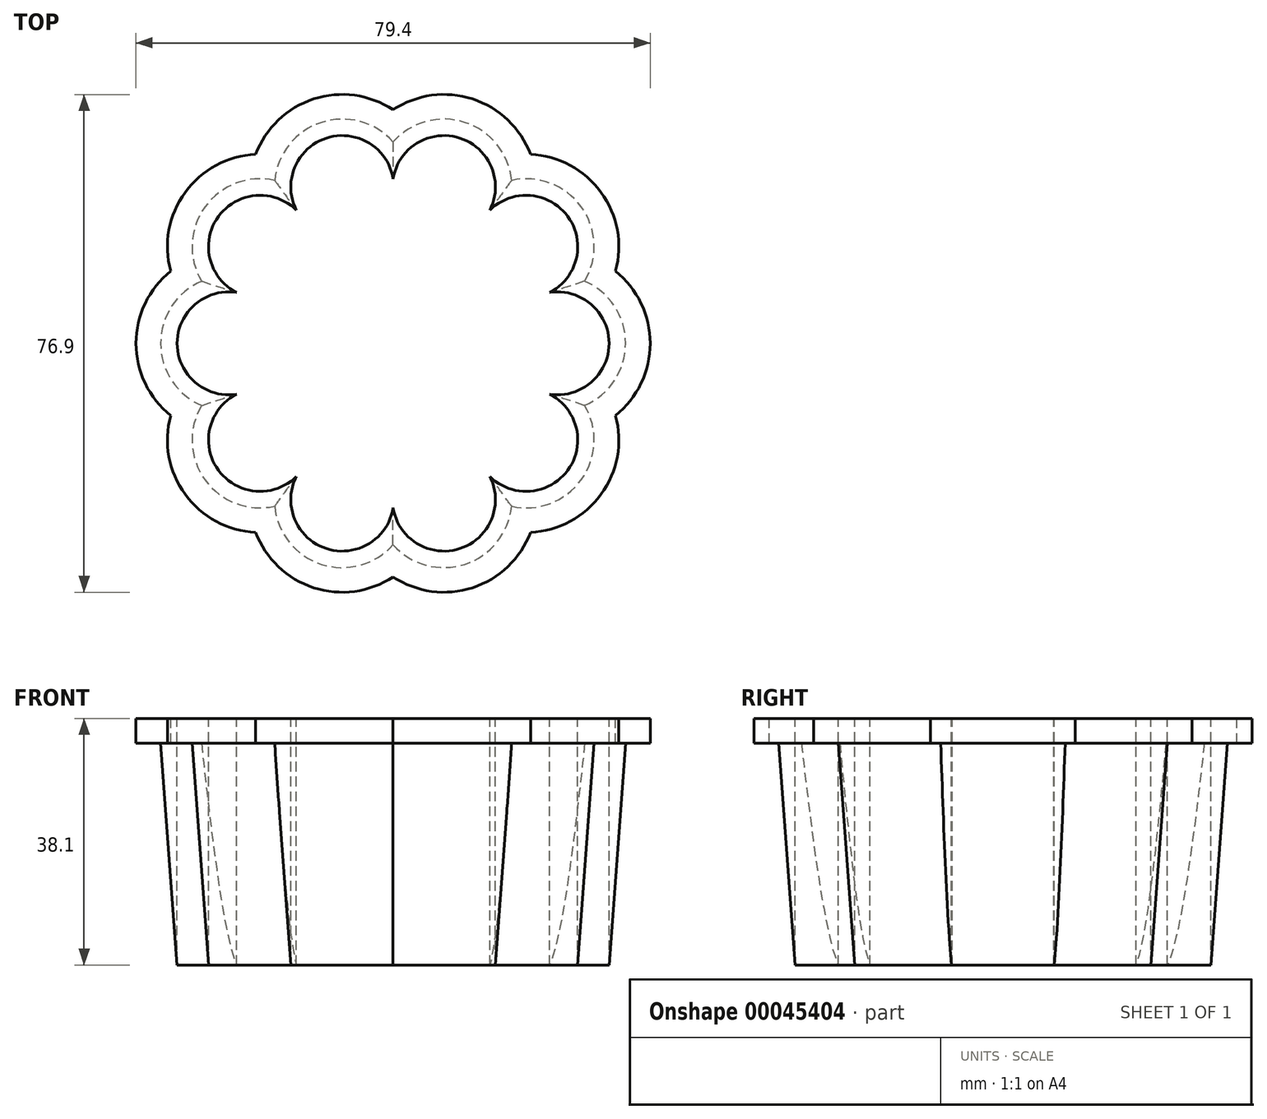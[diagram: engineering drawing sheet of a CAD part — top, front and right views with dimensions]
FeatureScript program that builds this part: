
annotation { "Feature Type Name" : "Feature", "Feature Type Description" : "" }
export const myFeature = defineFeature(function(context is Context, id is Id, definition is map)
    precondition{}
    {
        {
            var Q0;
            Q0=qCreatedBy(makeId("Top.planeOp"),FACE);
            var sketch = newSketch(context, id + "F0", { "sketchPlane" : qUnion([Q0])});
            skCircle(sketch, "E0", {"center": v(0, 0) * mm, "radius": 25.4 * mm, "construction": true});
            skArc(sketch, "E1", {"start": v(-24.16, -7.85) * mm, "mid": v(-26.98, -19.6) * mm, "end": v(-14.93, -20.55) * mm});
            skArc(sketch, "E2.1.0", {"start": v(-24.16, 7.85) * mm, "mid": v(-33.35, 0) * mm, "end": v(-24.16, -7.85) * mm});
            skArc(sketch, "E2.2.0", {"start": v(-14.93, 20.55) * mm, "mid": v(-26.98, 19.6) * mm, "end": v(-24.16, 7.85) * mm});
            skArc(sketch, "E2.3.0", {"start": v(0, 25.4) * mm, "mid": v(-10.3, 31.71) * mm, "end": v(-14.93, 20.55) * mm});
            skArc(sketch, "E2.4.0", {"start": v(14.93, 20.55) * mm, "mid": v(10.3, 31.71) * mm, "end": v(0, 25.4) * mm});
            skArc(sketch, "E2.5.0", {"start": v(24.16, 7.85) * mm, "mid": v(26.98, 19.6) * mm, "end": v(14.93, 20.55) * mm});
            skArc(sketch, "E2.6.0", {"start": v(24.16, -7.85) * mm, "mid": v(33.35, 0) * mm, "end": v(24.16, 7.85) * mm});
            skArc(sketch, "E2.7.0", {"start": v(14.93, -20.55) * mm, "mid": v(26.98, -19.6) * mm, "end": v(24.16, -7.85) * mm});
            skArc(sketch, "E2.8.0", {"start": v(0, -25.4) * mm, "mid": v(10.3, -31.71) * mm, "end": v(14.93, -20.55) * mm});
            skArc(sketch, "E2.9.0", {"start": v(-14.93, -20.55) * mm, "mid": v(-10.3, -31.71) * mm, "end": v(0, -25.4) * mm});
            skLineSegment(sketch, "E2.anchor1", {"start": v(0, 0) * mm, "end": v(-14.93, -20.55) * mm, "construction": true});
            skLineSegment(sketch, "E2.anchor2", {"start": v(0, 0) * mm, "end": v(0, -25.4) * mm, "construction": true});
            skLineSegment(sketch, "E3", {"start": v(-25.4, 0) * mm, "end": v(0, 0) * mm, "construction": true});
            skPoint(sketch, "E4", {"position": v(-33.35, 0) * mm});
            skSolve(sketch);
        }
        {
            var Q0;
            Q0=qCreatedBy(makeId("Front.planeOp"),FACE);
            var sketch = newSketch(context, id + "F1", { "sketchPlane" : qUnion([Q0])});
            skPoint(sketch, "E5.0", {"position": v(-33.35, 0) * mm});
            skLineSegment(sketch, "E6", {"start": v(-33.35, 0) * mm, "end": v(-33.35, 38.1) * mm});
            skLineSegment(sketch, "E7", {"start": v(-33.35, 38.1) * mm, "end": v(-39.7, 38.1) * mm});
            skLineSegment(sketch, "E8", {"start": v(-39.7, 38.1) * mm, "end": v(-39.7, 34.3) * mm});
            skLineSegment(sketch, "E9", {"start": v(-39.7, 34.3) * mm, "end": v(-35.89, 34.3) * mm});
            skLineSegment(sketch, "E10", {"start": v(-35.89, 34.3) * mm, "end": v(-33.35, 0) * mm});
            skSolve(sketch);
        }
        {
            var Q0;
            Q0=qSketchRegion(id+"F1",true);
            var Q1;
            Q1=qConstructionFilter(qBodyType(qCreatedBy(id+"F0",EDGE),BodyType.WIRE),ConstructionObject.NO);
            sweep(context, id + "F2", {"profiles" : qUnion([Q0]), "path" : qUnion([Q1])});
        }
    });
